# Revit family: Drain_Floor-Jay R.Smith-Round-Type-DX2566_Series
name_source: partatom
category: Plumbing Fixtures
units: mm (PartAtom-declared; Revit-internal decimal feet)

## family parameters
Always vertical = Yes
Cut with Voids When Loaded = No
OmniClass Number = 23.70.50.21.24
OmniClass Title = Waste Water Drains
Part Type = Normal
Room Calculation Point = No
Round Connector Dimension = Use Radius
Shared = No
Work Plane-Based = Yes

## types (6) — shared parameters
Assembly Code = D2030300
CW Connection = No
Default Elevation = 0"
Description = Wide Flange Floor Drains Safe-Set® Bucket
Diameter = 20"
Finish = Cast Iron-Jay R Smith-Duco Coated
G - Galvanized Cast Iron = No
HW Connection = No
Height = 9"
Height 1 = 5 1/2"
Height 2 = 8 3/4"
Height Constraint = 1/4"
Load Rating = 'Light Duty having a Safe Live (Static) Load less than 2,000 lbs. (900 kg) per ASME A112.6.3 Floor Drain Standard.
Manufacturer = Jay R. Smith
Material = Cast Iron-Jay R Smith-Duco Coated
NB - Nickel Bronze Top = No
NO-HUB Adaptor = No
PB - Polished Bronze Top = No
Product Documentation Link = https://www.jrsmith.com
Product Page URL = https://www.jrsmith.com
Quad Close Trap Seal = No
SH - Securing Holes = No
Strainer Diameter = 12 1/4"
T - Threaded Outlet = No
U - Vandal Proof Grate = No
URL = http://www.jrsmith.com
Vent Connection = No
Waste Connection = Yes

## per-type parameters (varying)
| type | Connection Radius | Connection Size | Outlet Connection Description |
| DX2566C 02 | 1" | 2" | 2" Caulk Outlet Connection |
| DX2566C 03 | 1 1/2" | 3" | 3" Caulk Outlet Connection |
| DX2566C 04 | 2" | 4" | 4" Caulk Outlet Connection |
| DX2566T 02 | 1" | 2" | 2" Threaded Outlet Connection |
| DX2566T 03 | 1 1/2" | 3" | 3" Threaded Outlet Connection |
| DX2566T 04 | 2" | 4" | 4" Threaded Outlet Connection |

note: column(s) folded — value = type name in every type: Model

## geometry (parser evidence)
native form markers: Sweep x3
no freeform markers — native parametric forms only
